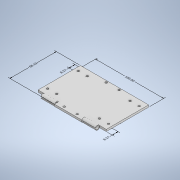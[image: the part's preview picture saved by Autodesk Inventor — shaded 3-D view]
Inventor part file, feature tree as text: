
AUTODESK INVENTOR PART (.ipt)
format: ipt  version: 2020 (Build 240168000, 168)  size: 279,040 bytes
history: native  units: mm
features: sketch x18, hole x12, other x11, extrude x6
ambient origin geometry x8: Origin, YZ Plane, XZ Plane, XY Plane, X Axis, Y Axis, Z Axis, Center Point
bodies: Solid1 (feature_tree)
feature tree (47):
  other  "Annotations"
  extrude  "Extrusion1"  Depth=62.1mm
  extrude  "Extrusion2"  Depth=40.0mm TaperAngle=0.0deg
  extrude  "Extrusion3"  Depth=6.0mm
  extrude  "Extrusion4"  Depth=61.39mm
  extrude  "Extrusion5"  Depth=6.0mm
  extrude  "Extrusion6"  Depth=10.0mm TaperAngle=0.0deg
  hole  "Hole1"  [1 undecoded]
  hole  "Hole2"  [1 undecoded]
  hole  "Hole3"  [1 undecoded]
  hole  "Hole4"  [1 undecoded]
  hole  "Hole5"  [1 undecoded]
  hole  "Hole6"  [1 undecoded]
  hole  "Hole7"  [1 undecoded]
  hole  "Hole8"  [1 undecoded]
  hole  "Hole10"  [1 undecoded]
  hole  "Hole9"  [1 undecoded]
  hole  "Hole12"  [1 undecoded]
  hole  "Hole11"  [1 undecoded]
  sketch  "Sketch1"  dims[d0=2.9mm d1=62.1mm]
  sketch  "Sketch3"  dims[d4=20.0mm d5=0.0mm d6=40.0mm d7=0.0mm]
  sketch  "Sketch4"  dims[d8=20.0mm d9=0.0mm]
  sketch  "Sketch5"  dims[d10=2.921mm d11=6.0mm d12=4.0mm d13=2.0mm d14=90.0deg d15=8.0mm d16=20.594885mm]
  sketch  "Sketch6"  dims[d17=2.921mm d18=6.0mm d19=4.0mm d20=2.0mm d21=90.0deg d22=8.0mm d23=20.594885mm]
  sketch  "Sketch7"  dims[d24=2.921mm d25=6.0mm d26=4.0mm d27=2.0mm d28=90.0deg d29=8.0mm d30=20.594885mm]
  sketch  "Sketch8"  dims[d31=2.921mm d32=6.0mm d33=4.0mm d34=2.0mm d35=90.0deg d36=8.0mm d37=20.594885mm d42=18.95mm]
  sketch  "Sketch9"  dims[d48=18.95mm d49=61.39mm]
  sketch  "Sketch10"  dims[d50=6.0mm d51=0.0mm d53=3.95mm]
  sketch  "Sketch11"  dims[d54=61.39mm d61=10.0mm d62=0.0mm]
  sketch  "Sketch12"  dims[d63=10.0mm d64=0.0mm]
  sketch  "Sketch13"  dims[d65=2.921mm d66=6.0mm d67=4.0mm d68=2.0mm d69=90.0deg d70=8.0mm d71=20.594885mm d80=40.525mm]
  sketch  "Sketch14"  dims[d81=3.95mm d82=40.525mm]
  sketch  "Sketch15"  dims[d84=2.921mm d85=6.0mm d86=4.0mm d87=2.0mm d88=90.0deg d89=8.0mm d90=20.594885mm]
  sketch  "Sketch16"  dims[d91=2.921mm d92=6.0mm d93=4.0mm d94=2.0mm d95=90.0deg d96=8.0mm d97=20.594885mm]
  sketch  "Sketch17"  dims[d98=2.921mm d99=6.0mm d100=4.0mm d101=2.0mm d102=90.0deg d103=8.0mm d104=20.594885mm]
  sketch  "Sketch18"  dims[d105=2.921mm d106=6.0mm d107=4.0mm d108=2.0mm d109=90.0deg d110=8.0mm d111=20.594885mm]
  sketch  "Sketch19"  dims[d112=2.921mm d113=6.0mm d114=4.0mm d115=2.0mm d116=90.0deg d117=8.0mm d118=20.594885mm d119=2.921mm d120=6.0mm d121=4.0mm d122=2.0mm d123=90.0deg d124=8.0mm d125=20.594885mm d126=2.921mm d127=6.0mm d128=4.0mm d129=2.0mm d130=90.0deg d131=8.0mm d132=20.594885mm d133=8.57mm d134=5.41mm d135=8.57mm d136=13.26mm d137=5.41mm d138=44.96mm d139=44.96mm d140=44.96mm d141=44.96mm d142=5.41mm d143=5.41mm d144=13.26mm d145=13.26mm d146=8.57mm d147=8.57mm d148=13.26mm d156=1.1mm d157=1.1mm d158=2.2mm d159=1.1mm d160=2.2mm d149=18.95mm d150=13.26mm d151=44.96mm d152=0.546068mm d153=8.57mm d154=5.128261mm d155=8.57mm d58=8.720877mm d59=0.837125mm d60=68.1mm d72=1.978463mm d73=6.235219mm d74=100.0mm d75=6.886257mm d76=40.525mm d77=1.822575mm d78=40.525mm d83=61.39mm]
  other  "Linear Dimension 5"
  other  "Linear Dimension 6"
  other  "Linear Dimension 7"
  other  "Linear Dimension 8"
  other  "Linear Dimension 9"
  other  "Linear Dimension 10"
  other  "Linear Dimension 11"
  other  "Linear Dimension 12"
  other  "Linear Dimension 13"
  other  "Linear Dimension 14"
note: 12 required parameter values undecoded (feature->parameter linkage not recoverable at this tier; creation-order binding heuristic only, values carry confidence <= 0.55)
